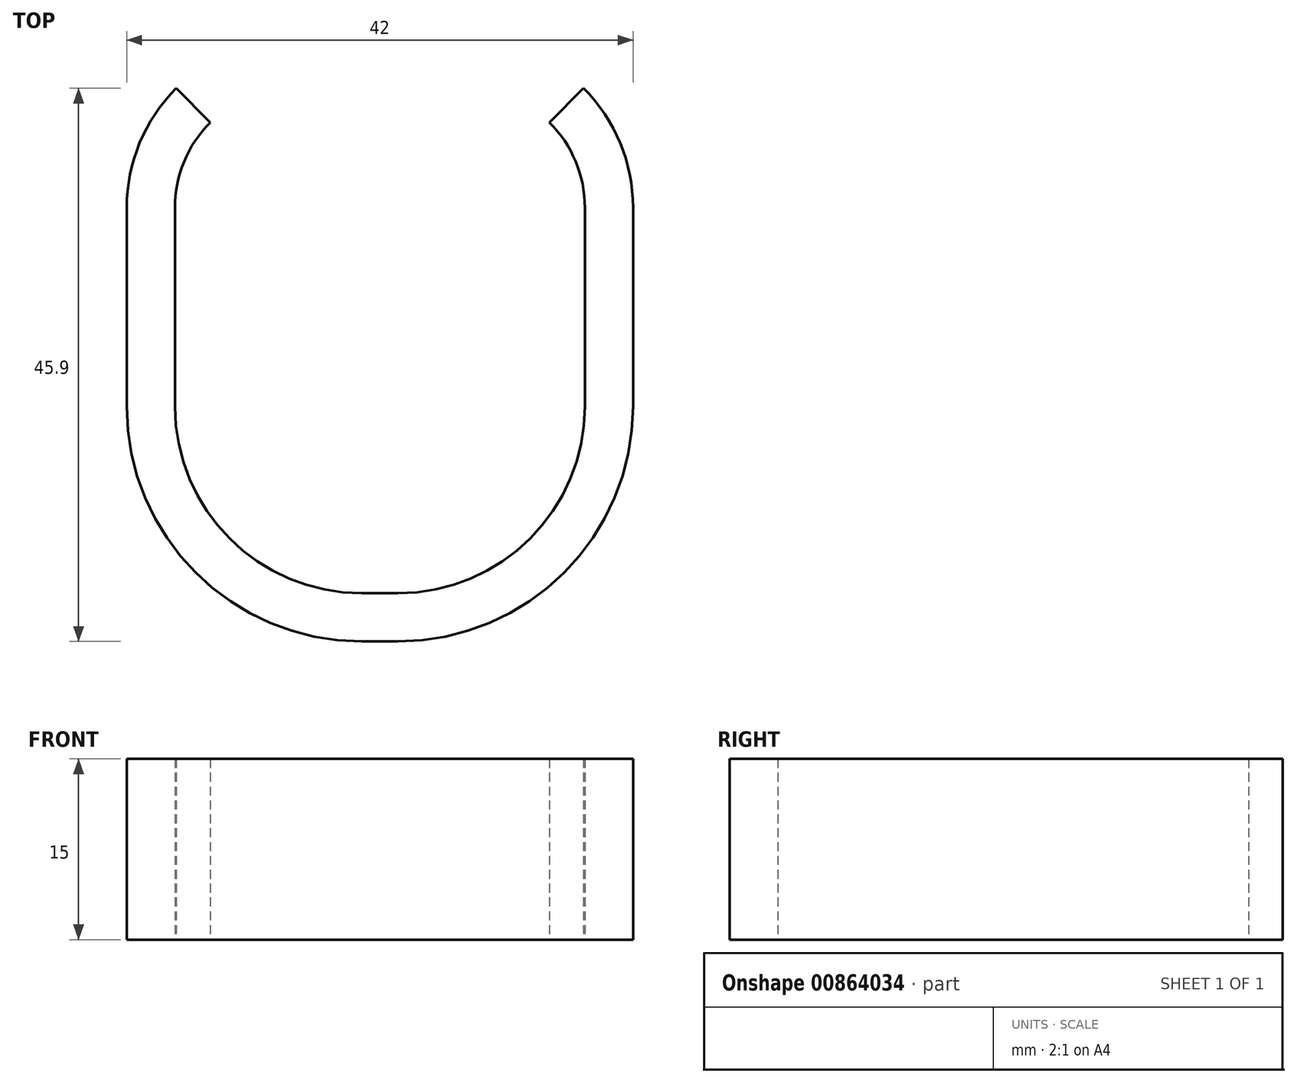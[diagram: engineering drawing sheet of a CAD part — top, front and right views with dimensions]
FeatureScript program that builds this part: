
annotation { "Feature Type Name" : "Feature", "Feature Type Description" : "" }
export const myFeature = defineFeature(function(context is Context, id is Id, definition is map)
    precondition{}
    {
        {
            var Q0;
            Q0=qCreatedBy(makeId("Top.planeOp"),FACE);
            var sketch = newSketch(context, id + "F0", { "sketchPlane" : qUnion([Q0])});
            skLineSegment(sketch, "E0.bottom", {"start": v(-7, 21) * mm, "end": v(7, 21) * mm});
            skLineSegment(sketch, "E0.top", {"start": v(-1.5, -21) * mm, "end": v(1.5, -21) * mm});
            skLineSegment(sketch, "E0.left", {"start": v(-17, 11) * mm, "end": v(-17, -5.5) * mm});
            skLineSegment(sketch, "E0.right", {"start": v(17, 11) * mm, "end": v(17, -5.5) * mm});
            skPoint(sketch, "E1.visualSharp", {"position": v(-17, -21) * mm});
            skArc(sketch, "E1.filletArc", {"start": v(-17, -5.5) * mm, "mid": v(-12.46, -16.46) * mm, "end": v(-1.5, -21) * mm});
            skArc(sketch, "E2.filletArc", {"start": v(17, 11) * mm, "mid": v(14.07, 18.07) * mm, "end": v(7, 21) * mm});
            skPoint(sketch, "E3.visualSharp", {"position": v(17, -21) * mm});
            skArc(sketch, "E3.filletArc", {"start": v(1.5, -21) * mm, "mid": v(12.46, -16.46) * mm, "end": v(17, -5.5) * mm});
            skArc(sketch, "E4.filletArc", {"start": v(-7, 21) * mm, "mid": v(-14.07, 18.07) * mm, "end": v(-17, 11) * mm});
            skLineSegment(sketch, "E5", {"start": v(-17, 11) * mm, "end": v(17, 11) * mm});
            skLineSegment(sketch, "E6", {"start": v(-7, 11) * mm, "end": v(-14.07, 18.07) * mm});
            skLineSegment(sketch, "E7", {"start": v(7, 11) * mm, "end": v(14.07, 18.07) * mm});
            skLineSegment(sketch, "E8", {"start": v(-17, 11) * mm, "end": v(-7, 11) * mm});
            skLineSegment(sketch, "E9", {"start": v(7, 11) * mm, "end": v(17, 11) * mm});
            skArc(sketch, "E10", {"start": v(-17, 11) * mm, "mid": v(-16.24, 14.83) * mm, "end": v(-14.07, 18.07) * mm});
            skArc(sketch, "E11", {"start": v(17, 11) * mm, "mid": v(16.24, 14.83) * mm, "end": v(14.07, 18.07) * mm});
            skArc(sketch, "E12.0", {"start": v(-21, 11) * mm, "mid": v(-19.93, 16.36) * mm, "end": v(-16.9, 20.9) * mm});
            skLineSegment(sketch, "E12.1", {"start": v(-21, 11) * mm, "end": v(-21, -5.5) * mm});
            skArc(sketch, "E12.2", {"start": v(-21, -5.5) * mm, "mid": v(-15.29, -19.29) * mm, "end": v(-1.5, -25) * mm});
            skArc(sketch, "E12.3", {"start": v(21, 11) * mm, "mid": v(19.93, 16.36) * mm, "end": v(16.9, 20.9) * mm});
            skLineSegment(sketch, "E12.4", {"start": v(21, 11) * mm, "end": v(21, -5.5) * mm});
            skArc(sketch, "E12.5", {"start": v(1.5, -25) * mm, "mid": v(15.29, -19.29) * mm, "end": v(21, -5.5) * mm});
            skLineSegment(sketch, "E12.6", {"start": v(-1.5, -25) * mm, "end": v(1.5, -25) * mm});
            skLineSegment(sketch, "E13", {"start": v(-16.9, 20.9) * mm, "end": v(-14.07, 18.07) * mm});
            skLineSegment(sketch, "E14", {"start": v(14.07, 18.07) * mm, "end": v(16.9, 20.9) * mm});
            skSolve(sketch);
        }
        {
            var Q0;
            Q0=makeQuery(id+"F0.imprint","IMPRINT",FACE,{"disambiguationData":[TD([[makeQuery(id+"F0.imprint","IMPRINT",EDGE,{"derivedFrom":sQuery(id+"F0.wireOp",EDGE,"E0.top")}),-1.0]])]});
            extrude(context, id + "F1", {"entities" : qUnion([Q0]), "depth" : 15 * mm, "offsetDistance" : 25 * mm});
        }
    });
